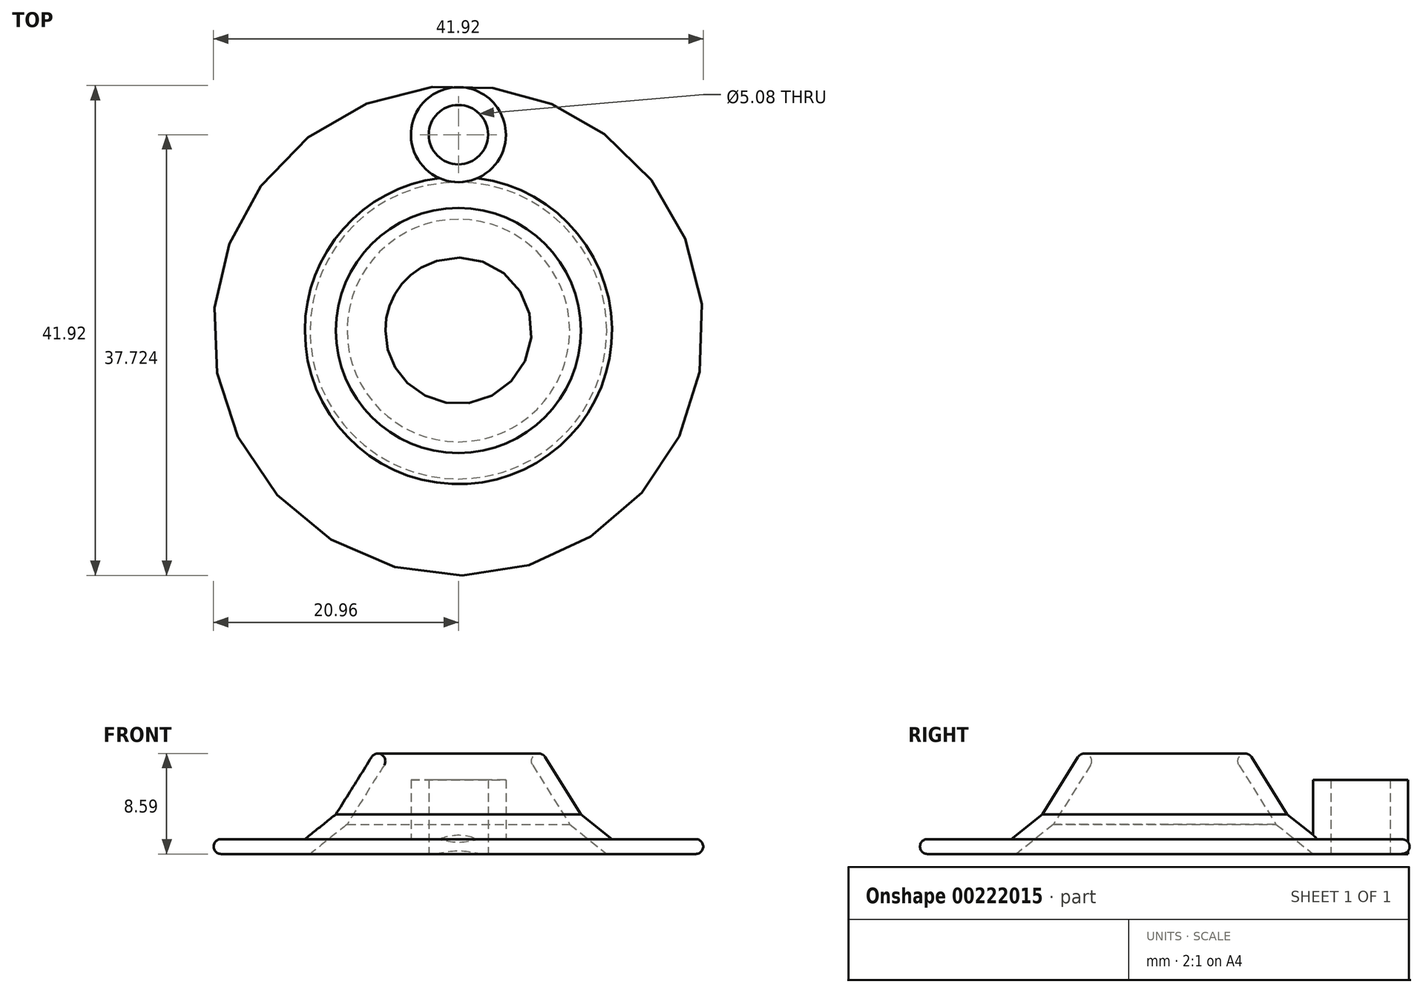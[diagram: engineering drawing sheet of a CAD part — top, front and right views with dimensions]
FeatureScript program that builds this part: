
annotation { "Feature Type Name" : "Feature", "Feature Type Description" : "" }
export const myFeature = defineFeature(function(context is Context, id is Id, definition is map)
    precondition{}
    {
        {
            var Q0;
            Q0=qCreatedBy(makeId("Front.planeOp"),FACE);
            var sketch = newSketch(context, id + "F0", { "sketchPlane" : qUnion([Q0])});
            skLineSegment(sketch, "E0", {"start": v(20.32, 0) * mm, "end": v(12.7, 0) * mm});
            skLineSegment(sketch, "E1", {"start": v(12.7, 0) * mm, "end": v(9.53, 2.54) * mm});
            skLineSegment(sketch, "E2", {"start": v(9.53, 2.54) * mm, "end": v(6.35, 7.62) * mm});
            skArc(sketch, "E3", {"start": v(7.43, 8.3) * mm, "mid": v(6.55, 8.5) * mm, "end": v(6.35, 7.62) * mm});
            skLineSegment(sketch, "E4", {"start": v(20.32, 1.27) * mm, "end": v(13.15, 1.27) * mm});
            skLineSegment(sketch, "E5", {"start": v(7.43, 8.3) * mm, "end": v(10.49, 3.4) * mm});
            skLineSegment(sketch, "E6", {"start": v(10.49, 3.4) * mm, "end": v(13.15, 1.27) * mm});
            skLineSegment(sketch, "E7", {"start": v(0, 0) * mm, "end": v(0, 6.07) * mm});
            skArc(sketch, "E8", {"start": v(20.32, 0) * mm, "mid": v(20.96, 0.64) * mm, "end": v(20.32, 1.27) * mm});
            skSolve(sketch);
        }
        {
            var Q0;
            Q0 = qSketchRegion(id + "F0", true);
            var Q1;
            Q1=sQuery(id+"F0.wireOp",EDGE,"E7");
            revolve(context, id + "F1", {"entities" : qUnion([Q0]), "axis" : qUnion([Q1]), "revolveType" : RevolveType.FULL});
        }
        {
            var Q0;
            Q0=qCreatedBy(makeId("Top.planeOp"),FACE);
            var sketch = newSketch(context, id + "F2", { "sketchPlane" : qUnion([Q0])});
            skCircle(sketch, "E9", {"center": v(0, 16.76) * mm, "radius": 4.06 * mm});
            skCircle(sketch, "E10", {"center": v(0, 16.76) * mm, "radius": 2.54 * mm});
            skSolve(sketch);
        }
        {
            var Q0;
            Q0 = qSketchRegion(id + "F2", true);
            extrude(context, id + "F3", {"entities" : qUnion([Q0]), "operationType" : NewBodyOperationType.ADD, "depth" : 6.35 * mm});
        }
        {
            var Q0;
            Q0=qCreatedBy(makeId("Top.planeOp"),FACE);
            var sketch = newSketch(context, id + "F4", { "sketchPlane" : qUnion([Q0])});
            skCircle(sketch, "E11", {"center": v(0, 16.76) * mm, "radius": 2.54 * mm});
            skSolve(sketch);
        }
        {
            var Q0;
            Q0 = qSketchRegion(id + "F4", true);
            extrude(context, id + "F5", {"entities" : qUnion([Q0]), "operationType" : NewBodyOperationType.REMOVE, "oppositeDirection" : true, "depth" : 6.35 * mm, "hasSecondDirection" : true, "secondDirectionOppositeDirection" : false, "secondDirectionDepth" : 6.35 * mm});
        }
    });
